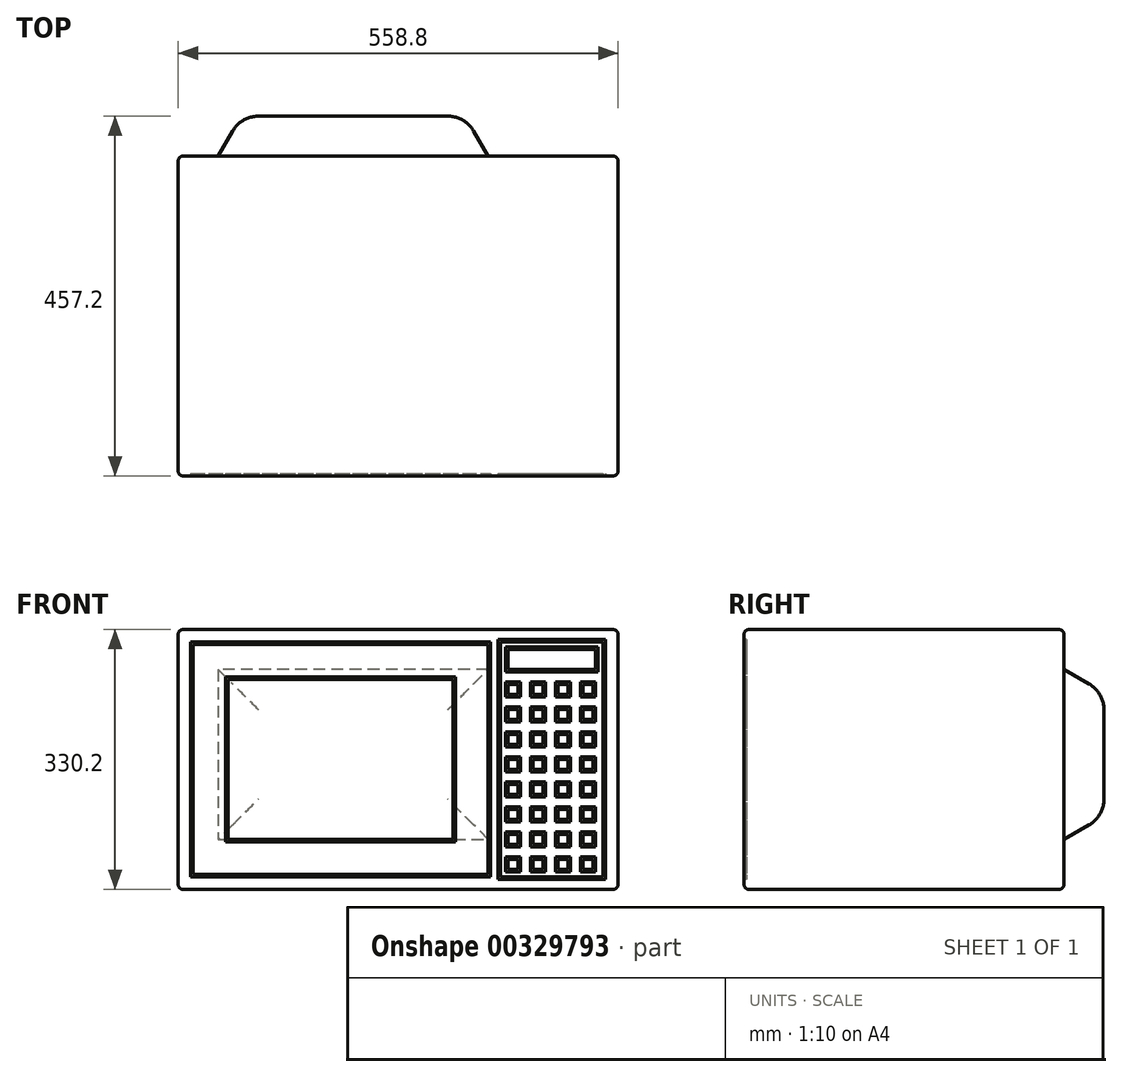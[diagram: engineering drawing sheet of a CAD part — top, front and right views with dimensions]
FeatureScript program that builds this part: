
annotation { "Feature Type Name" : "Feature", "Feature Type Description" : "" }
export const myFeature = defineFeature(function(context is Context, id is Id, definition is map)
    precondition{}
    {
        {
            var Q0;
            Q0=qCreatedBy(makeId("Front.planeOp"),FACE);
            var sketch = newSketch(context, id + "F0", { "sketchPlane" : qUnion([Q0])});
            skLineSegment(sketch, "E0.bottom", {"start": v(0, 0) * mm, "end": v(-558.8, 0) * mm});
            skLineSegment(sketch, "E0.top", {"start": v(0, 330.2) * mm, "end": v(-558.8, 330.2) * mm});
            skLineSegment(sketch, "E0.left", {"start": v(0, 0) * mm, "end": v(0, 330.2) * mm});
            skLineSegment(sketch, "E0.right", {"start": v(-558.8, 0) * mm, "end": v(-558.8, 330.2) * mm});
            skSolve(sketch);
        }
        {
            var Q0;
            Q0 = qSketchRegion(id + "F0", true);
            extrude(context, id + "F1", {"entities" : qUnion([Q0]), "oppositeDirection" : true, "depth" : 406.4 * mm});
        }
        {
            var Q0;
            Q0=makeQuery(id+"F1.opExtrude","SWEPT_FACE",FACE,{"disambiguationData":[OSD([sQuery(id+"F0.wireOp",EDGE,"E0.top")])]});
            var Q1;
            Q1=makeQuery(id+"F1.opExtrude","SWEPT_FACE",FACE,{"disambiguationData":[OSD([sQuery(id+"F0.wireOp",EDGE,"E0.left")])]});
            var Q2;
            Q2=makeQuery(id+"F1.opExtrude","CAP_FACE",FACE,{"disambiguationData":[OSD([sQuery(id+"F0.wireOp",EDGE,"E0.bottom"),sQuery(id+"F0.wireOp",EDGE,"E0.top"),sQuery(id+"F0.wireOp",EDGE,"E0.left"),sQuery(id+"F0.wireOp",EDGE,"E0.right")])],"isStart":false});
            var Q3;
            Q3=makeQuery(id+"F1.opExtrude","CAP_FACE",FACE,{"disambiguationData":[OSD([sQuery(id+"F0.wireOp",EDGE,"E0.bottom"),sQuery(id+"F0.wireOp",EDGE,"E0.top"),sQuery(id+"F0.wireOp",EDGE,"E0.left"),sQuery(id+"F0.wireOp",EDGE,"E0.right")])],"isStart":true});
            var Q4;
            Q4=makeQuery(id+"F1.opExtrude","SWEPT_FACE",FACE,{"disambiguationData":[OSD([sQuery(id+"F0.wireOp",EDGE,"E0.right")])]});
            fillet(context, id + "F2", {"entities" : qUnion([Q0, Q1, Q2, Q3, Q4]), "radius" : 6.35 * mm, "tangentPropagation" : true, "allowEdgeOverflow" : false});
        }
        {
            var Q0;
            Q0=makeQuery(id+"F1.opExtrude","CAP_FACE",FACE,{"disambiguationData":[OSD([sQuery(id+"F0.wireOp",EDGE,"E0.bottom"),sQuery(id+"F0.wireOp",EDGE,"E0.top"),sQuery(id+"F0.wireOp",EDGE,"E0.left"),sQuery(id+"F0.wireOp",EDGE,"E0.right")])],"isStart":false});
            var sketch = newSketch(context, id + "F3", { "sketchPlane" : qUnion([Q0])});
            skLineSegment(sketch, "E1.bottom", {"start": v(508, 279.4) * mm, "end": v(165.1, 279.4) * mm});
            skLineSegment(sketch, "E1.top", {"start": v(508, 63.5) * mm, "end": v(165.1, 63.5) * mm});
            skLineSegment(sketch, "E1.left", {"start": v(508, 279.4) * mm, "end": v(508, 63.5) * mm});
            skLineSegment(sketch, "E1.right", {"start": v(165.1, 279.4) * mm, "end": v(165.1, 63.5) * mm});
            skSolve(sketch);
        }
        {
            var Q0;
            Q0 = qSketchRegion(id + "F3", true);
            extrude(context, id + "F4", {"entities" : qUnion([Q0]), "operationType" : NewBodyOperationType.ADD, "depth" : 50.8 * mm, "hasDraft" : true, "draftAngle" : 30 * degree, "draftPullDirection" : true});
        }
        {
            var Q0;
            Q0=makeQuery(id+"F4.opExtrude","CAP_FACE",FACE,{"disambiguationData":[OSD([sQuery(id+"F3.wireOp",EDGE,"E1.bottom"),sQuery(id+"F3.wireOp",EDGE,"E1.top"),sQuery(id+"F3.wireOp",EDGE,"E1.left"),sQuery(id+"F3.wireOp",EDGE,"E1.right")])],"isStart":false});
            var Q1;
            Q1=makeQuery(id+"F4.opExtrude","CAP_EDGE",EDGE,{"disambiguationData":[OSD([sQuery(id+"F3.wireOp",EDGE,"E1.bottom")])],"isStart":true});
            var Q2;
            Q2=makeQuery(id+"F4.opExtrude","CAP_EDGE",EDGE,{"disambiguationData":[OSD([sQuery(id+"F3.wireOp",EDGE,"E1.left")])],"isStart":true});
            var Q3;
            Q3=makeQuery(id+"F4.opExtrude","CAP_EDGE",EDGE,{"disambiguationData":[OSD([sQuery(id+"F3.wireOp",EDGE,"E1.right")])],"isStart":true});
            var Q4;
            Q4=makeQuery(id+"F4.opExtrude","CAP_EDGE",EDGE,{"disambiguationData":[OSD([sQuery(id+"F3.wireOp",EDGE,"E1.top")])],"isStart":true});
            fillet(context, id + "F5", {"entities" : qUnion([Q0, Q1, Q2, Q3, Q4]), "radius" : 38.1 * mm, "tangentPropagation" : true, "allowEdgeOverflow" : false});
        }
        {
            var Q0;
            Q0=makeQuery(id+"F1.opExtrude","CAP_FACE",FACE,{"disambiguationData":[OSD([sQuery(id+"F0.wireOp",EDGE,"E0.bottom"),sQuery(id+"F0.wireOp",EDGE,"E0.top"),sQuery(id+"F0.wireOp",EDGE,"E0.left"),sQuery(id+"F0.wireOp",EDGE,"E0.right")])],"isStart":true});
            var sketch = newSketch(context, id + "F6", { "sketchPlane" : qUnion([Q0])});
            skLineSegment(sketch, "E2.bottom", {"start": v(-542.93, 314.33) * mm, "end": v(-161.93, 314.33) * mm});
            skLineSegment(sketch, "E2.top", {"start": v(-542.93, 15.88) * mm, "end": v(-161.92, 15.88) * mm});
            skLineSegment(sketch, "E2.left", {"start": v(-542.93, 314.32) * mm, "end": v(-542.93, 15.87) * mm});
            skLineSegment(sketch, "E2.right", {"start": v(-161.93, 314.33) * mm, "end": v(-161.92, 15.88) * mm});
            skLineSegment(sketch, "E3.bottom", {"start": v(-498.48, 269.88) * mm, "end": v(-206.38, 269.88) * mm});
            skLineSegment(sketch, "E3.top", {"start": v(-498.48, 60.32) * mm, "end": v(-206.37, 60.33) * mm});
            skLineSegment(sketch, "E3.left", {"start": v(-498.48, 269.88) * mm, "end": v(-498.48, 60.32) * mm});
            skLineSegment(sketch, "E3.right", {"start": v(-206.38, 269.88) * mm, "end": v(-206.37, 60.33) * mm});
            skLineSegment(sketch, "E4.bottom", {"start": v(-149.23, 314.33) * mm, "end": v(-19.05, 314.33) * mm});
            skLineSegment(sketch, "E4.top", {"start": v(-149.22, 15.88) * mm, "end": v(-19.05, 15.88) * mm});
            skLineSegment(sketch, "E4.left", {"start": v(-149.23, 314.33) * mm, "end": v(-149.22, 15.88) * mm});
            skLineSegment(sketch, "E4.right", {"start": v(-19.05, 314.33) * mm, "end": v(-19.05, 15.88) * mm});
            skLineSegment(sketch, "E5.bottom", {"start": v(-142.88, 307.98) * mm, "end": v(-25.4, 307.98) * mm});
            skLineSegment(sketch, "E5.top", {"start": v(-142.88, 276.23) * mm, "end": v(-25.4, 276.23) * mm});
            skLineSegment(sketch, "E5.left", {"start": v(-142.88, 307.98) * mm, "end": v(-142.88, 276.23) * mm});
            skLineSegment(sketch, "E5.right", {"start": v(-25.4, 307.98) * mm, "end": v(-25.4, 276.23) * mm});
            skLineSegment(sketch, "E6.bottom", {"start": v(-142.87, 41.28) * mm, "end": v(-123.83, 41.28) * mm});
            skLineSegment(sketch, "E6.top", {"start": v(-142.87, 22.23) * mm, "end": v(-123.83, 22.23) * mm});
            skLineSegment(sketch, "E6.left", {"start": v(-142.87, 41.28) * mm, "end": v(-142.87, 22.23) * mm});
            skLineSegment(sketch, "E6.right", {"start": v(-123.83, 41.28) * mm, "end": v(-123.83, 22.23) * mm});
            skLineSegment(sketch, "E7.0", {"start": v(-539.75, 311.15) * mm, "end": v(-539.75, 19.05) * mm});
            skLineSegment(sketch, "E7.1", {"start": v(-539.75, 311.15) * mm, "end": v(-165.1, 311.15) * mm});
            skLineSegment(sketch, "E7.2", {"start": v(-165.1, 311.15) * mm, "end": v(-165.1, 19.05) * mm});
            skLineSegment(sketch, "E7.3", {"start": v(-539.75, 19.05) * mm, "end": v(-165.1, 19.05) * mm});
            skLineSegment(sketch, "E8.0", {"start": v(-495.3, 266.7) * mm, "end": v(-209.55, 266.7) * mm});
            skLineSegment(sketch, "E8.1", {"start": v(-495.3, 266.7) * mm, "end": v(-495.3, 63.5) * mm});
            skLineSegment(sketch, "E8.2", {"start": v(-495.3, 63.5) * mm, "end": v(-209.55, 63.5) * mm});
            skLineSegment(sketch, "E8.3", {"start": v(-209.55, 266.7) * mm, "end": v(-209.55, 63.5) * mm});
            skLineSegment(sketch, "E9.0", {"start": v(-152.4, 317.5) * mm, "end": v(-15.88, 317.5) * mm});
            skLineSegment(sketch, "E9.1", {"start": v(-152.4, 317.5) * mm, "end": v(-152.4, 12.7) * mm});
            skLineSegment(sketch, "E9.2", {"start": v(-152.4, 12.7) * mm, "end": v(-15.88, 12.7) * mm});
            skLineSegment(sketch, "E9.3", {"start": v(-15.88, 317.5) * mm, "end": v(-15.88, 12.7) * mm});
            skLineSegment(sketch, "E10.0", {"start": v(-139.7, 279.4) * mm, "end": v(-28.58, 279.4) * mm});
            skLineSegment(sketch, "E10.1", {"start": v(-139.7, 304.8) * mm, "end": v(-139.7, 279.4) * mm});
            skLineSegment(sketch, "E10.2", {"start": v(-139.7, 304.8) * mm, "end": v(-28.58, 304.8) * mm});
            skLineSegment(sketch, "E10.3", {"start": v(-28.58, 304.8) * mm, "end": v(-28.58, 279.4) * mm});
            skLineSegment(sketch, "E11.0", {"start": v(-127, 38.1) * mm, "end": v(-127, 25.4) * mm});
            skLineSegment(sketch, "E11.1", {"start": v(-139.7, 38.1) * mm, "end": v(-127, 38.1) * mm});
            skLineSegment(sketch, "E11.2", {"start": v(-139.7, 38.1) * mm, "end": v(-139.7, 25.4) * mm});
            skLineSegment(sketch, "E11.3", {"start": v(-139.7, 25.4) * mm, "end": v(-127, 25.4) * mm});
            skLineSegment(sketch, "E12.0.1.0", {"start": v(-142.87, 73.03) * mm, "end": v(-142.87, 53.98) * mm});
            skLineSegment(sketch, "E12.0.1.1", {"start": v(-139.7, 69.85) * mm, "end": v(-139.7, 57.15) * mm});
            skLineSegment(sketch, "E12.0.1.2", {"start": v(-142.87, 73.03) * mm, "end": v(-123.83, 73.03) * mm});
            skLineSegment(sketch, "E12.0.1.3", {"start": v(-139.7, 69.85) * mm, "end": v(-127, 69.85) * mm});
            skLineSegment(sketch, "E12.0.1.4", {"start": v(-123.83, 73.03) * mm, "end": v(-123.83, 53.98) * mm});
            skLineSegment(sketch, "E12.0.1.5", {"start": v(-127, 69.85) * mm, "end": v(-127, 57.15) * mm});
            skLineSegment(sketch, "E12.0.1.6", {"start": v(-139.7, 57.15) * mm, "end": v(-127, 57.15) * mm});
            skLineSegment(sketch, "E12.0.1.7", {"start": v(-142.87, 53.98) * mm, "end": v(-123.83, 53.98) * mm});
            skLineSegment(sketch, "E12.0.2.0", {"start": v(-142.87, 104.78) * mm, "end": v(-142.87, 85.73) * mm});
            skLineSegment(sketch, "E12.0.2.1", {"start": v(-139.7, 101.6) * mm, "end": v(-139.7, 88.9) * mm});
            skLineSegment(sketch, "E12.0.2.2", {"start": v(-142.87, 104.78) * mm, "end": v(-123.83, 104.78) * mm});
            skLineSegment(sketch, "E12.0.2.3", {"start": v(-139.7, 101.6) * mm, "end": v(-127, 101.6) * mm});
            skLineSegment(sketch, "E12.0.2.4", {"start": v(-123.83, 104.78) * mm, "end": v(-123.83, 85.73) * mm});
            skLineSegment(sketch, "E12.0.2.5", {"start": v(-127, 101.6) * mm, "end": v(-127, 88.9) * mm});
            skLineSegment(sketch, "E12.0.2.6", {"start": v(-139.7, 88.9) * mm, "end": v(-127, 88.9) * mm});
            skLineSegment(sketch, "E12.0.2.7", {"start": v(-142.87, 85.73) * mm, "end": v(-123.83, 85.73) * mm});
            skLineSegment(sketch, "E12.0.3.0", {"start": v(-142.87, 136.53) * mm, "end": v(-142.87, 117.48) * mm});
            skLineSegment(sketch, "E12.0.3.1", {"start": v(-139.7, 133.35) * mm, "end": v(-139.7, 120.65) * mm});
            skLineSegment(sketch, "E12.0.3.2", {"start": v(-142.87, 136.53) * mm, "end": v(-123.83, 136.53) * mm});
            skLineSegment(sketch, "E12.0.3.3", {"start": v(-139.7, 133.35) * mm, "end": v(-127, 133.35) * mm});
            skLineSegment(sketch, "E12.0.3.4", {"start": v(-123.83, 136.53) * mm, "end": v(-123.83, 117.48) * mm});
            skLineSegment(sketch, "E12.0.3.5", {"start": v(-127, 133.35) * mm, "end": v(-127, 120.65) * mm});
            skLineSegment(sketch, "E12.0.3.6", {"start": v(-139.7, 120.65) * mm, "end": v(-127, 120.65) * mm});
            skLineSegment(sketch, "E12.0.3.7", {"start": v(-142.87, 117.48) * mm, "end": v(-123.83, 117.48) * mm});
            skLineSegment(sketch, "E12.0.4.0", {"start": v(-142.87, 168.28) * mm, "end": v(-142.87, 149.23) * mm});
            skLineSegment(sketch, "E12.0.4.1", {"start": v(-139.7, 165.1) * mm, "end": v(-139.7, 152.4) * mm});
            skLineSegment(sketch, "E12.0.4.2", {"start": v(-142.87, 168.28) * mm, "end": v(-123.83, 168.28) * mm});
            skLineSegment(sketch, "E12.0.4.3", {"start": v(-139.7, 165.1) * mm, "end": v(-127, 165.1) * mm});
            skLineSegment(sketch, "E12.0.4.4", {"start": v(-123.83, 168.28) * mm, "end": v(-123.83, 149.23) * mm});
            skLineSegment(sketch, "E12.0.4.5", {"start": v(-127, 165.1) * mm, "end": v(-127, 152.4) * mm});
            skLineSegment(sketch, "E12.0.4.6", {"start": v(-139.7, 152.4) * mm, "end": v(-127, 152.4) * mm});
            skLineSegment(sketch, "E12.0.4.7", {"start": v(-142.87, 149.23) * mm, "end": v(-123.83, 149.23) * mm});
            skLineSegment(sketch, "E12.0.5.0", {"start": v(-142.87, 200.03) * mm, "end": v(-142.87, 180.98) * mm});
            skLineSegment(sketch, "E12.0.5.1", {"start": v(-139.7, 196.85) * mm, "end": v(-139.7, 184.15) * mm});
            skLineSegment(sketch, "E12.0.5.2", {"start": v(-142.87, 200.03) * mm, "end": v(-123.83, 200.03) * mm});
            skLineSegment(sketch, "E12.0.5.3", {"start": v(-139.7, 196.85) * mm, "end": v(-127, 196.85) * mm});
            skLineSegment(sketch, "E12.0.5.4", {"start": v(-123.83, 200.03) * mm, "end": v(-123.83, 180.98) * mm});
            skLineSegment(sketch, "E12.0.5.5", {"start": v(-127, 196.85) * mm, "end": v(-127, 184.15) * mm});
            skLineSegment(sketch, "E12.0.5.6", {"start": v(-139.7, 184.15) * mm, "end": v(-127, 184.15) * mm});
            skLineSegment(sketch, "E12.0.5.7", {"start": v(-142.87, 180.98) * mm, "end": v(-123.83, 180.98) * mm});
            skLineSegment(sketch, "E12.0.6.0", {"start": v(-142.87, 231.78) * mm, "end": v(-142.87, 212.73) * mm});
            skLineSegment(sketch, "E12.0.6.1", {"start": v(-139.7, 228.6) * mm, "end": v(-139.7, 215.9) * mm});
            skLineSegment(sketch, "E12.0.6.2", {"start": v(-142.87, 231.78) * mm, "end": v(-123.83, 231.78) * mm});
            skLineSegment(sketch, "E12.0.6.3", {"start": v(-139.7, 228.6) * mm, "end": v(-127, 228.6) * mm});
            skLineSegment(sketch, "E12.0.6.4", {"start": v(-123.83, 231.78) * mm, "end": v(-123.83, 212.73) * mm});
            skLineSegment(sketch, "E12.0.6.5", {"start": v(-127, 228.6) * mm, "end": v(-127, 215.9) * mm});
            skLineSegment(sketch, "E12.0.6.6", {"start": v(-139.7, 215.9) * mm, "end": v(-127, 215.9) * mm});
            skLineSegment(sketch, "E12.0.6.7", {"start": v(-142.87, 212.73) * mm, "end": v(-123.83, 212.73) * mm});
            skLineSegment(sketch, "E12.0.7.0", {"start": v(-142.87, 263.53) * mm, "end": v(-142.87, 244.48) * mm});
            skLineSegment(sketch, "E12.0.7.1", {"start": v(-139.7, 260.35) * mm, "end": v(-139.7, 247.65) * mm});
            skLineSegment(sketch, "E12.0.7.2", {"start": v(-142.87, 263.53) * mm, "end": v(-123.83, 263.53) * mm});
            skLineSegment(sketch, "E12.0.7.3", {"start": v(-139.7, 260.35) * mm, "end": v(-127, 260.35) * mm});
            skLineSegment(sketch, "E12.0.7.4", {"start": v(-123.83, 263.53) * mm, "end": v(-123.83, 244.48) * mm});
            skLineSegment(sketch, "E12.0.7.5", {"start": v(-127, 260.35) * mm, "end": v(-127, 247.65) * mm});
            skLineSegment(sketch, "E12.0.7.6", {"start": v(-139.7, 247.65) * mm, "end": v(-127, 247.65) * mm});
            skLineSegment(sketch, "E12.0.7.7", {"start": v(-142.87, 244.48) * mm, "end": v(-123.83, 244.48) * mm});
            skLineSegment(sketch, "E12.1.0.0", {"start": v(-111.12, 41.28) * mm, "end": v(-111.12, 22.23) * mm});
            skLineSegment(sketch, "E12.1.0.1", {"start": v(-107.95, 38.1) * mm, "end": v(-107.95, 25.4) * mm});
            skLineSegment(sketch, "E12.1.0.2", {"start": v(-111.12, 41.28) * mm, "end": v(-92.08, 41.28) * mm});
            skLineSegment(sketch, "E12.1.0.3", {"start": v(-107.95, 38.1) * mm, "end": v(-95.25, 38.1) * mm});
            skLineSegment(sketch, "E12.1.0.4", {"start": v(-92.08, 41.28) * mm, "end": v(-92.08, 22.23) * mm});
            skLineSegment(sketch, "E12.1.0.5", {"start": v(-95.25, 38.1) * mm, "end": v(-95.25, 25.4) * mm});
            skLineSegment(sketch, "E12.1.0.6", {"start": v(-107.95, 25.4) * mm, "end": v(-95.25, 25.4) * mm});
            skLineSegment(sketch, "E12.1.0.7", {"start": v(-111.12, 22.23) * mm, "end": v(-92.08, 22.23) * mm});
            skLineSegment(sketch, "E12.1.1.0", {"start": v(-111.12, 73.03) * mm, "end": v(-111.12, 53.98) * mm});
            skLineSegment(sketch, "E12.1.1.1", {"start": v(-107.95, 69.85) * mm, "end": v(-107.95, 57.15) * mm});
            skLineSegment(sketch, "E12.1.1.2", {"start": v(-111.12, 73.03) * mm, "end": v(-92.08, 73.03) * mm});
            skLineSegment(sketch, "E12.1.1.3", {"start": v(-107.95, 69.85) * mm, "end": v(-95.25, 69.85) * mm});
            skLineSegment(sketch, "E12.1.1.4", {"start": v(-92.08, 73.03) * mm, "end": v(-92.08, 53.98) * mm});
            skLineSegment(sketch, "E12.1.1.5", {"start": v(-95.25, 69.85) * mm, "end": v(-95.25, 57.15) * mm});
            skLineSegment(sketch, "E12.1.1.6", {"start": v(-107.95, 57.15) * mm, "end": v(-95.25, 57.15) * mm});
            skLineSegment(sketch, "E12.1.1.7", {"start": v(-111.12, 53.98) * mm, "end": v(-92.08, 53.98) * mm});
            skLineSegment(sketch, "E12.1.2.0", {"start": v(-111.12, 104.78) * mm, "end": v(-111.12, 85.73) * mm});
            skLineSegment(sketch, "E12.1.2.1", {"start": v(-107.95, 101.6) * mm, "end": v(-107.95, 88.9) * mm});
            skLineSegment(sketch, "E12.1.2.2", {"start": v(-111.12, 104.78) * mm, "end": v(-92.08, 104.78) * mm});
            skLineSegment(sketch, "E12.1.2.3", {"start": v(-107.95, 101.6) * mm, "end": v(-95.25, 101.6) * mm});
            skLineSegment(sketch, "E12.1.2.4", {"start": v(-92.08, 104.78) * mm, "end": v(-92.08, 85.73) * mm});
            skLineSegment(sketch, "E12.1.2.5", {"start": v(-95.25, 101.6) * mm, "end": v(-95.25, 88.9) * mm});
            skLineSegment(sketch, "E12.1.2.6", {"start": v(-107.95, 88.9) * mm, "end": v(-95.25, 88.9) * mm});
            skLineSegment(sketch, "E12.1.2.7", {"start": v(-111.12, 85.73) * mm, "end": v(-92.08, 85.73) * mm});
            skLineSegment(sketch, "E12.1.3.0", {"start": v(-111.12, 136.53) * mm, "end": v(-111.12, 117.48) * mm});
            skLineSegment(sketch, "E12.1.3.1", {"start": v(-107.95, 133.35) * mm, "end": v(-107.95, 120.65) * mm});
            skLineSegment(sketch, "E12.1.3.2", {"start": v(-111.12, 136.53) * mm, "end": v(-92.08, 136.53) * mm});
            skLineSegment(sketch, "E12.1.3.3", {"start": v(-107.95, 133.35) * mm, "end": v(-95.25, 133.35) * mm});
            skLineSegment(sketch, "E12.1.3.4", {"start": v(-92.08, 136.53) * mm, "end": v(-92.08, 117.48) * mm});
            skLineSegment(sketch, "E12.1.3.5", {"start": v(-95.25, 133.35) * mm, "end": v(-95.25, 120.65) * mm});
            skLineSegment(sketch, "E12.1.3.6", {"start": v(-107.95, 120.65) * mm, "end": v(-95.25, 120.65) * mm});
            skLineSegment(sketch, "E12.1.3.7", {"start": v(-111.12, 117.48) * mm, "end": v(-92.08, 117.48) * mm});
            skLineSegment(sketch, "E12.1.4.0", {"start": v(-111.12, 168.28) * mm, "end": v(-111.12, 149.23) * mm});
            skLineSegment(sketch, "E12.1.4.1", {"start": v(-107.95, 165.1) * mm, "end": v(-107.95, 152.4) * mm});
            skLineSegment(sketch, "E12.1.4.2", {"start": v(-111.12, 168.28) * mm, "end": v(-92.08, 168.28) * mm});
            skLineSegment(sketch, "E12.1.4.3", {"start": v(-107.95, 165.1) * mm, "end": v(-95.25, 165.1) * mm});
            skLineSegment(sketch, "E12.1.4.4", {"start": v(-92.08, 168.28) * mm, "end": v(-92.08, 149.23) * mm});
            skLineSegment(sketch, "E12.1.4.5", {"start": v(-95.25, 165.1) * mm, "end": v(-95.25, 152.4) * mm});
            skLineSegment(sketch, "E12.1.4.6", {"start": v(-107.95, 152.4) * mm, "end": v(-95.25, 152.4) * mm});
            skLineSegment(sketch, "E12.1.4.7", {"start": v(-111.12, 149.23) * mm, "end": v(-92.08, 149.23) * mm});
            skLineSegment(sketch, "E12.1.5.0", {"start": v(-111.12, 200.03) * mm, "end": v(-111.12, 180.98) * mm});
            skLineSegment(sketch, "E12.1.5.1", {"start": v(-107.95, 196.85) * mm, "end": v(-107.95, 184.15) * mm});
            skLineSegment(sketch, "E12.1.5.2", {"start": v(-111.12, 200.03) * mm, "end": v(-92.08, 200.03) * mm});
            skLineSegment(sketch, "E12.1.5.3", {"start": v(-107.95, 196.85) * mm, "end": v(-95.25, 196.85) * mm});
            skLineSegment(sketch, "E12.1.5.4", {"start": v(-92.08, 200.03) * mm, "end": v(-92.08, 180.98) * mm});
            skLineSegment(sketch, "E12.1.5.5", {"start": v(-95.25, 196.85) * mm, "end": v(-95.25, 184.15) * mm});
            skLineSegment(sketch, "E12.1.5.6", {"start": v(-107.95, 184.15) * mm, "end": v(-95.25, 184.15) * mm});
            skLineSegment(sketch, "E12.1.5.7", {"start": v(-111.12, 180.98) * mm, "end": v(-92.08, 180.98) * mm});
            skLineSegment(sketch, "E12.1.6.0", {"start": v(-111.12, 231.78) * mm, "end": v(-111.12, 212.73) * mm});
            skLineSegment(sketch, "E12.1.6.1", {"start": v(-107.95, 228.6) * mm, "end": v(-107.95, 215.9) * mm});
            skLineSegment(sketch, "E12.1.6.2", {"start": v(-111.12, 231.78) * mm, "end": v(-92.08, 231.78) * mm});
            skLineSegment(sketch, "E12.1.6.3", {"start": v(-107.95, 228.6) * mm, "end": v(-95.25, 228.6) * mm});
            skLineSegment(sketch, "E12.1.6.4", {"start": v(-92.08, 231.78) * mm, "end": v(-92.08, 212.73) * mm});
            skLineSegment(sketch, "E12.1.6.5", {"start": v(-95.25, 228.6) * mm, "end": v(-95.25, 215.9) * mm});
            skLineSegment(sketch, "E12.1.6.6", {"start": v(-107.95, 215.9) * mm, "end": v(-95.25, 215.9) * mm});
            skLineSegment(sketch, "E12.1.6.7", {"start": v(-111.12, 212.73) * mm, "end": v(-92.08, 212.73) * mm});
            skLineSegment(sketch, "E12.1.7.0", {"start": v(-111.12, 263.53) * mm, "end": v(-111.12, 244.48) * mm});
            skLineSegment(sketch, "E12.1.7.1", {"start": v(-107.95, 260.35) * mm, "end": v(-107.95, 247.65) * mm});
            skLineSegment(sketch, "E12.1.7.2", {"start": v(-111.12, 263.53) * mm, "end": v(-92.08, 263.53) * mm});
            skLineSegment(sketch, "E12.1.7.3", {"start": v(-107.95, 260.35) * mm, "end": v(-95.25, 260.35) * mm});
            skLineSegment(sketch, "E12.1.7.4", {"start": v(-92.08, 263.53) * mm, "end": v(-92.08, 244.48) * mm});
            skLineSegment(sketch, "E12.1.7.5", {"start": v(-95.25, 260.35) * mm, "end": v(-95.25, 247.65) * mm});
            skLineSegment(sketch, "E12.1.7.6", {"start": v(-107.95, 247.65) * mm, "end": v(-95.25, 247.65) * mm});
            skLineSegment(sketch, "E12.1.7.7", {"start": v(-111.12, 244.48) * mm, "end": v(-92.08, 244.48) * mm});
            skLineSegment(sketch, "E12.2.0.0", {"start": v(-79.37, 41.28) * mm, "end": v(-79.37, 22.23) * mm});
            skLineSegment(sketch, "E12.2.0.1", {"start": v(-76.2, 38.1) * mm, "end": v(-76.2, 25.4) * mm});
            skLineSegment(sketch, "E12.2.0.2", {"start": v(-79.37, 41.28) * mm, "end": v(-60.33, 41.28) * mm});
            skLineSegment(sketch, "E12.2.0.3", {"start": v(-76.2, 38.1) * mm, "end": v(-63.5, 38.1) * mm});
            skLineSegment(sketch, "E12.2.0.4", {"start": v(-60.33, 41.28) * mm, "end": v(-60.33, 22.23) * mm});
            skLineSegment(sketch, "E12.2.0.5", {"start": v(-63.5, 38.1) * mm, "end": v(-63.5, 25.4) * mm});
            skLineSegment(sketch, "E12.2.0.6", {"start": v(-76.2, 25.4) * mm, "end": v(-63.5, 25.4) * mm});
            skLineSegment(sketch, "E12.2.0.7", {"start": v(-79.37, 22.23) * mm, "end": v(-60.33, 22.23) * mm});
            skLineSegment(sketch, "E12.2.1.0", {"start": v(-79.37, 73.03) * mm, "end": v(-79.37, 53.98) * mm});
            skLineSegment(sketch, "E12.2.1.1", {"start": v(-76.2, 69.85) * mm, "end": v(-76.2, 57.15) * mm});
            skLineSegment(sketch, "E12.2.1.2", {"start": v(-79.37, 73.03) * mm, "end": v(-60.33, 73.03) * mm});
            skLineSegment(sketch, "E12.2.1.3", {"start": v(-76.2, 69.85) * mm, "end": v(-63.5, 69.85) * mm});
            skLineSegment(sketch, "E12.2.1.4", {"start": v(-60.33, 73.03) * mm, "end": v(-60.33, 53.98) * mm});
            skLineSegment(sketch, "E12.2.1.5", {"start": v(-63.5, 69.85) * mm, "end": v(-63.5, 57.15) * mm});
            skLineSegment(sketch, "E12.2.1.6", {"start": v(-76.2, 57.15) * mm, "end": v(-63.5, 57.15) * mm});
            skLineSegment(sketch, "E12.2.1.7", {"start": v(-79.37, 53.98) * mm, "end": v(-60.33, 53.98) * mm});
            skLineSegment(sketch, "E12.2.2.0", {"start": v(-79.37, 104.78) * mm, "end": v(-79.37, 85.73) * mm});
            skLineSegment(sketch, "E12.2.2.1", {"start": v(-76.2, 101.6) * mm, "end": v(-76.2, 88.9) * mm});
            skLineSegment(sketch, "E12.2.2.2", {"start": v(-79.37, 104.78) * mm, "end": v(-60.33, 104.78) * mm});
            skLineSegment(sketch, "E12.2.2.3", {"start": v(-76.2, 101.6) * mm, "end": v(-63.5, 101.6) * mm});
            skLineSegment(sketch, "E12.2.2.4", {"start": v(-60.33, 104.78) * mm, "end": v(-60.33, 85.73) * mm});
            skLineSegment(sketch, "E12.2.2.5", {"start": v(-63.5, 101.6) * mm, "end": v(-63.5, 88.9) * mm});
            skLineSegment(sketch, "E12.2.2.6", {"start": v(-76.2, 88.9) * mm, "end": v(-63.5, 88.9) * mm});
            skLineSegment(sketch, "E12.2.2.7", {"start": v(-79.37, 85.73) * mm, "end": v(-60.33, 85.73) * mm});
            skLineSegment(sketch, "E12.2.3.0", {"start": v(-79.37, 136.53) * mm, "end": v(-79.37, 117.48) * mm});
            skLineSegment(sketch, "E12.2.3.1", {"start": v(-76.2, 133.35) * mm, "end": v(-76.2, 120.65) * mm});
            skLineSegment(sketch, "E12.2.3.2", {"start": v(-79.37, 136.53) * mm, "end": v(-60.33, 136.53) * mm});
            skLineSegment(sketch, "E12.2.3.3", {"start": v(-76.2, 133.35) * mm, "end": v(-63.5, 133.35) * mm});
            skLineSegment(sketch, "E12.2.3.4", {"start": v(-60.33, 136.53) * mm, "end": v(-60.33, 117.48) * mm});
            skLineSegment(sketch, "E12.2.3.5", {"start": v(-63.5, 133.35) * mm, "end": v(-63.5, 120.65) * mm});
            skLineSegment(sketch, "E12.2.3.6", {"start": v(-76.2, 120.65) * mm, "end": v(-63.5, 120.65) * mm});
            skLineSegment(sketch, "E12.2.3.7", {"start": v(-79.37, 117.48) * mm, "end": v(-60.33, 117.48) * mm});
            skLineSegment(sketch, "E12.2.4.0", {"start": v(-79.37, 168.28) * mm, "end": v(-79.37, 149.23) * mm});
            skLineSegment(sketch, "E12.2.4.1", {"start": v(-76.2, 165.1) * mm, "end": v(-76.2, 152.4) * mm});
            skLineSegment(sketch, "E12.2.4.2", {"start": v(-79.37, 168.28) * mm, "end": v(-60.33, 168.28) * mm});
            skLineSegment(sketch, "E12.2.4.3", {"start": v(-76.2, 165.1) * mm, "end": v(-63.5, 165.1) * mm});
            skLineSegment(sketch, "E12.2.4.4", {"start": v(-60.33, 168.28) * mm, "end": v(-60.33, 149.23) * mm});
            skLineSegment(sketch, "E12.2.4.5", {"start": v(-63.5, 165.1) * mm, "end": v(-63.5, 152.4) * mm});
            skLineSegment(sketch, "E12.2.4.6", {"start": v(-76.2, 152.4) * mm, "end": v(-63.5, 152.4) * mm});
            skLineSegment(sketch, "E12.2.4.7", {"start": v(-79.37, 149.23) * mm, "end": v(-60.33, 149.23) * mm});
            skLineSegment(sketch, "E12.2.5.0", {"start": v(-79.37, 200.03) * mm, "end": v(-79.37, 180.98) * mm});
            skLineSegment(sketch, "E12.2.5.1", {"start": v(-76.2, 196.85) * mm, "end": v(-76.2, 184.15) * mm});
            skLineSegment(sketch, "E12.2.5.2", {"start": v(-79.37, 200.03) * mm, "end": v(-60.33, 200.03) * mm});
            skLineSegment(sketch, "E12.2.5.3", {"start": v(-76.2, 196.85) * mm, "end": v(-63.5, 196.85) * mm});
            skLineSegment(sketch, "E12.2.5.4", {"start": v(-60.33, 200.03) * mm, "end": v(-60.33, 180.98) * mm});
            skLineSegment(sketch, "E12.2.5.5", {"start": v(-63.5, 196.85) * mm, "end": v(-63.5, 184.15) * mm});
            skLineSegment(sketch, "E12.2.5.6", {"start": v(-76.2, 184.15) * mm, "end": v(-63.5, 184.15) * mm});
            skLineSegment(sketch, "E12.2.5.7", {"start": v(-79.37, 180.98) * mm, "end": v(-60.33, 180.98) * mm});
            skLineSegment(sketch, "E12.2.6.0", {"start": v(-79.37, 231.78) * mm, "end": v(-79.37, 212.73) * mm});
            skLineSegment(sketch, "E12.2.6.1", {"start": v(-76.2, 228.6) * mm, "end": v(-76.2, 215.9) * mm});
            skLineSegment(sketch, "E12.2.6.2", {"start": v(-79.37, 231.78) * mm, "end": v(-60.33, 231.78) * mm});
            skLineSegment(sketch, "E12.2.6.3", {"start": v(-76.2, 228.6) * mm, "end": v(-63.5, 228.6) * mm});
            skLineSegment(sketch, "E12.2.6.4", {"start": v(-60.33, 231.78) * mm, "end": v(-60.33, 212.73) * mm});
            skLineSegment(sketch, "E12.2.6.5", {"start": v(-63.5, 228.6) * mm, "end": v(-63.5, 215.9) * mm});
            skLineSegment(sketch, "E12.2.6.6", {"start": v(-76.2, 215.9) * mm, "end": v(-63.5, 215.9) * mm});
            skLineSegment(sketch, "E12.2.6.7", {"start": v(-79.37, 212.73) * mm, "end": v(-60.33, 212.73) * mm});
            skLineSegment(sketch, "E12.2.7.0", {"start": v(-79.37, 263.53) * mm, "end": v(-79.37, 244.48) * mm});
            skLineSegment(sketch, "E12.2.7.1", {"start": v(-76.2, 260.35) * mm, "end": v(-76.2, 247.65) * mm});
            skLineSegment(sketch, "E12.2.7.2", {"start": v(-79.37, 263.53) * mm, "end": v(-60.33, 263.53) * mm});
            skLineSegment(sketch, "E12.2.7.3", {"start": v(-76.2, 260.35) * mm, "end": v(-63.5, 260.35) * mm});
            skLineSegment(sketch, "E12.2.7.4", {"start": v(-60.33, 263.53) * mm, "end": v(-60.33, 244.48) * mm});
            skLineSegment(sketch, "E12.2.7.5", {"start": v(-63.5, 260.35) * mm, "end": v(-63.5, 247.65) * mm});
            skLineSegment(sketch, "E12.2.7.6", {"start": v(-76.2, 247.65) * mm, "end": v(-63.5, 247.65) * mm});
            skLineSegment(sketch, "E12.2.7.7", {"start": v(-79.37, 244.48) * mm, "end": v(-60.33, 244.48) * mm});
            skLineSegment(sketch, "E12.3.0.0", {"start": v(-47.62, 41.28) * mm, "end": v(-47.62, 22.23) * mm});
            skLineSegment(sketch, "E12.3.0.1", {"start": v(-44.45, 38.1) * mm, "end": v(-44.45, 25.4) * mm});
            skLineSegment(sketch, "E12.3.0.2", {"start": v(-47.62, 41.28) * mm, "end": v(-28.58, 41.28) * mm});
            skLineSegment(sketch, "E12.3.0.3", {"start": v(-44.45, 38.1) * mm, "end": v(-31.75, 38.1) * mm});
            skLineSegment(sketch, "E12.3.0.4", {"start": v(-28.58, 41.28) * mm, "end": v(-28.58, 22.23) * mm});
            skLineSegment(sketch, "E12.3.0.5", {"start": v(-31.75, 38.1) * mm, "end": v(-31.75, 25.4) * mm});
            skLineSegment(sketch, "E12.3.0.6", {"start": v(-44.45, 25.4) * mm, "end": v(-31.75, 25.4) * mm});
            skLineSegment(sketch, "E12.3.0.7", {"start": v(-47.62, 22.23) * mm, "end": v(-28.58, 22.23) * mm});
            skLineSegment(sketch, "E12.3.1.0", {"start": v(-47.62, 73.03) * mm, "end": v(-47.62, 53.98) * mm});
            skLineSegment(sketch, "E12.3.1.1", {"start": v(-44.45, 69.85) * mm, "end": v(-44.45, 57.15) * mm});
            skLineSegment(sketch, "E12.3.1.2", {"start": v(-47.62, 73.03) * mm, "end": v(-28.58, 73.03) * mm});
            skLineSegment(sketch, "E12.3.1.3", {"start": v(-44.45, 69.85) * mm, "end": v(-31.75, 69.85) * mm});
            skLineSegment(sketch, "E12.3.1.4", {"start": v(-28.58, 73.03) * mm, "end": v(-28.58, 53.98) * mm});
            skLineSegment(sketch, "E12.3.1.5", {"start": v(-31.75, 69.85) * mm, "end": v(-31.75, 57.15) * mm});
            skLineSegment(sketch, "E12.3.1.6", {"start": v(-44.45, 57.15) * mm, "end": v(-31.75, 57.15) * mm});
            skLineSegment(sketch, "E12.3.1.7", {"start": v(-47.62, 53.98) * mm, "end": v(-28.58, 53.98) * mm});
            skLineSegment(sketch, "E12.3.2.0", {"start": v(-47.62, 104.78) * mm, "end": v(-47.62, 85.73) * mm});
            skLineSegment(sketch, "E12.3.2.1", {"start": v(-44.45, 101.6) * mm, "end": v(-44.45, 88.9) * mm});
            skLineSegment(sketch, "E12.3.2.2", {"start": v(-47.62, 104.78) * mm, "end": v(-28.58, 104.78) * mm});
            skLineSegment(sketch, "E12.3.2.3", {"start": v(-44.45, 101.6) * mm, "end": v(-31.75, 101.6) * mm});
            skLineSegment(sketch, "E12.3.2.4", {"start": v(-28.58, 104.78) * mm, "end": v(-28.58, 85.73) * mm});
            skLineSegment(sketch, "E12.3.2.5", {"start": v(-31.75, 101.6) * mm, "end": v(-31.75, 88.9) * mm});
            skLineSegment(sketch, "E12.3.2.6", {"start": v(-44.45, 88.9) * mm, "end": v(-31.75, 88.9) * mm});
            skLineSegment(sketch, "E12.3.2.7", {"start": v(-47.62, 85.73) * mm, "end": v(-28.58, 85.73) * mm});
            skLineSegment(sketch, "E12.3.3.0", {"start": v(-47.62, 136.53) * mm, "end": v(-47.62, 117.48) * mm});
            skLineSegment(sketch, "E12.3.3.1", {"start": v(-44.45, 133.35) * mm, "end": v(-44.45, 120.65) * mm});
            skLineSegment(sketch, "E12.3.3.2", {"start": v(-47.62, 136.53) * mm, "end": v(-28.58, 136.53) * mm});
            skLineSegment(sketch, "E12.3.3.3", {"start": v(-44.45, 133.35) * mm, "end": v(-31.75, 133.35) * mm});
            skLineSegment(sketch, "E12.3.3.4", {"start": v(-28.58, 136.53) * mm, "end": v(-28.58, 117.48) * mm});
            skLineSegment(sketch, "E12.3.3.5", {"start": v(-31.75, 133.35) * mm, "end": v(-31.75, 120.65) * mm});
            skLineSegment(sketch, "E12.3.3.6", {"start": v(-44.45, 120.65) * mm, "end": v(-31.75, 120.65) * mm});
            skLineSegment(sketch, "E12.3.3.7", {"start": v(-47.62, 117.48) * mm, "end": v(-28.58, 117.48) * mm});
            skLineSegment(sketch, "E12.3.4.0", {"start": v(-47.62, 168.28) * mm, "end": v(-47.62, 149.23) * mm});
            skLineSegment(sketch, "E12.3.4.1", {"start": v(-44.45, 165.1) * mm, "end": v(-44.45, 152.4) * mm});
            skLineSegment(sketch, "E12.3.4.2", {"start": v(-47.62, 168.28) * mm, "end": v(-28.58, 168.28) * mm});
            skLineSegment(sketch, "E12.3.4.3", {"start": v(-44.45, 165.1) * mm, "end": v(-31.75, 165.1) * mm});
            skLineSegment(sketch, "E12.3.4.4", {"start": v(-28.58, 168.28) * mm, "end": v(-28.58, 149.23) * mm});
            skLineSegment(sketch, "E12.3.4.5", {"start": v(-31.75, 165.1) * mm, "end": v(-31.75, 152.4) * mm});
            skLineSegment(sketch, "E12.3.4.6", {"start": v(-44.45, 152.4) * mm, "end": v(-31.75, 152.4) * mm});
            skLineSegment(sketch, "E12.3.4.7", {"start": v(-47.62, 149.23) * mm, "end": v(-28.58, 149.23) * mm});
            skLineSegment(sketch, "E12.3.5.0", {"start": v(-47.62, 200.03) * mm, "end": v(-47.62, 180.98) * mm});
            skLineSegment(sketch, "E12.3.5.1", {"start": v(-44.45, 196.85) * mm, "end": v(-44.45, 184.15) * mm});
            skLineSegment(sketch, "E12.3.5.2", {"start": v(-47.62, 200.03) * mm, "end": v(-28.58, 200.03) * mm});
            skLineSegment(sketch, "E12.3.5.3", {"start": v(-44.45, 196.85) * mm, "end": v(-31.75, 196.85) * mm});
            skLineSegment(sketch, "E12.3.5.4", {"start": v(-28.58, 200.03) * mm, "end": v(-28.58, 180.98) * mm});
            skLineSegment(sketch, "E12.3.5.5", {"start": v(-31.75, 196.85) * mm, "end": v(-31.75, 184.15) * mm});
            skLineSegment(sketch, "E12.3.5.6", {"start": v(-44.45, 184.15) * mm, "end": v(-31.75, 184.15) * mm});
            skLineSegment(sketch, "E12.3.5.7", {"start": v(-47.62, 180.98) * mm, "end": v(-28.58, 180.98) * mm});
            skLineSegment(sketch, "E12.3.6.0", {"start": v(-47.62, 231.78) * mm, "end": v(-47.62, 212.73) * mm});
            skLineSegment(sketch, "E12.3.6.1", {"start": v(-44.45, 228.6) * mm, "end": v(-44.45, 215.9) * mm});
            skLineSegment(sketch, "E12.3.6.2", {"start": v(-47.62, 231.78) * mm, "end": v(-28.58, 231.78) * mm});
            skLineSegment(sketch, "E12.3.6.3", {"start": v(-44.45, 228.6) * mm, "end": v(-31.75, 228.6) * mm});
            skLineSegment(sketch, "E12.3.6.4", {"start": v(-28.58, 231.78) * mm, "end": v(-28.58, 212.73) * mm});
            skLineSegment(sketch, "E12.3.6.5", {"start": v(-31.75, 228.6) * mm, "end": v(-31.75, 215.9) * mm});
            skLineSegment(sketch, "E12.3.6.6", {"start": v(-44.45, 215.9) * mm, "end": v(-31.75, 215.9) * mm});
            skLineSegment(sketch, "E12.3.6.7", {"start": v(-47.62, 212.73) * mm, "end": v(-28.58, 212.73) * mm});
            skLineSegment(sketch, "E12.3.7.0", {"start": v(-47.62, 263.53) * mm, "end": v(-47.62, 244.48) * mm});
            skLineSegment(sketch, "E12.3.7.1", {"start": v(-44.45, 260.35) * mm, "end": v(-44.45, 247.65) * mm});
            skLineSegment(sketch, "E12.3.7.2", {"start": v(-47.62, 263.53) * mm, "end": v(-28.58, 263.53) * mm});
            skLineSegment(sketch, "E12.3.7.3", {"start": v(-44.45, 260.35) * mm, "end": v(-31.75, 260.35) * mm});
            skLineSegment(sketch, "E12.3.7.4", {"start": v(-28.58, 263.53) * mm, "end": v(-28.58, 244.48) * mm});
            skLineSegment(sketch, "E12.3.7.5", {"start": v(-31.75, 260.35) * mm, "end": v(-31.75, 247.65) * mm});
            skLineSegment(sketch, "E12.3.7.6", {"start": v(-44.45, 247.65) * mm, "end": v(-31.75, 247.65) * mm});
            skLineSegment(sketch, "E12.3.7.7", {"start": v(-47.62, 244.48) * mm, "end": v(-28.58, 244.48) * mm});
            skLineSegment(sketch, "E12.direction1", {"start": v(-142.87, 22.23) * mm, "end": v(-111.12, 22.23) * mm, "construction": true});
            skLineSegment(sketch, "E12.direction2", {"start": v(-142.87, 22.23) * mm, "end": v(-142.87, 53.98) * mm, "construction": true});
            skSolve(sketch);
        }
        {
            var Q0;
            Q0=makeQuery(id+"F6.imprint","IMPRINT",FACE,{"disambiguationData":[TD([[makeQuery(id+"F6.imprint","IMPRINT",EDGE,{"derivedFrom":sQuery(id+"F6.wireOp",EDGE,"E2.bottom")}),-1.0]])]});
            var Q1;
            Q1=makeQuery(id+"F6.imprint","IMPRINT",FACE,{"disambiguationData":[TD([[makeQuery(id+"F6.imprint","IMPRINT",EDGE,{"derivedFrom":sQuery(id+"F6.wireOp",EDGE,"E3.bottom")}),-1.0]])]});
            var Q2;
            Q2=makeQuery(id+"F6.imprint","IMPRINT",FACE,{"disambiguationData":[TD([[makeQuery(id+"F6.imprint","IMPRINT",EDGE,{"derivedFrom":sQuery(id+"F6.wireOp",EDGE,"E4.bottom")}),1.0]])]});
            var Q3;
            Q3=makeQuery(id+"F6.imprint","IMPRINT",FACE,{"disambiguationData":[TD([[makeQuery(id+"F6.imprint","IMPRINT",EDGE,{"derivedFrom":sQuery(id+"F6.wireOp",EDGE,"E5.bottom")}),-1.0]])]});
            var Q4;
            Q4=makeQuery(id+"F6.imprint","IMPRINT",FACE,{"disambiguationData":[TD([[makeQuery(id+"F6.imprint","IMPRINT",EDGE,{"derivedFrom":sQuery(id+"F6.wireOp",EDGE,"E12.0.7.0")}),1.0]])]});
            var Q5;
            Q5=makeQuery(id+"F6.imprint","IMPRINT",FACE,{"disambiguationData":[TD([[makeQuery(id+"F6.imprint","IMPRINT",EDGE,{"derivedFrom":sQuery(id+"F6.wireOp",EDGE,"E12.1.7.0")}),1.0]])]});
            var Q6;
            Q6=makeQuery(id+"F6.imprint","IMPRINT",FACE,{"disambiguationData":[TD([[makeQuery(id+"F6.imprint","IMPRINT",EDGE,{"derivedFrom":sQuery(id+"F6.wireOp",EDGE,"E12.2.7.0")}),1.0]])]});
            var Q7;
            Q7=makeQuery(id+"F6.imprint","IMPRINT",FACE,{"disambiguationData":[TD([[makeQuery(id+"F6.imprint","IMPRINT",EDGE,{"derivedFrom":sQuery(id+"F6.wireOp",EDGE,"E12.3.7.0")}),1.0]])]});
            var Q8;
            Q8=makeQuery(id+"F6.imprint","IMPRINT",FACE,{"disambiguationData":[TD([[makeQuery(id+"F6.imprint","IMPRINT",EDGE,{"derivedFrom":sQuery(id+"F6.wireOp",EDGE,"E12.3.6.0")}),1.0]])]});
            var Q9;
            Q9=makeQuery(id+"F6.imprint","IMPRINT",FACE,{"disambiguationData":[TD([[makeQuery(id+"F6.imprint","IMPRINT",EDGE,{"derivedFrom":sQuery(id+"F6.wireOp",EDGE,"E12.2.6.0")}),1.0]])]});
            var Q10;
            Q10=makeQuery(id+"F6.imprint","IMPRINT",FACE,{"disambiguationData":[TD([[makeQuery(id+"F6.imprint","IMPRINT",EDGE,{"derivedFrom":sQuery(id+"F6.wireOp",EDGE,"E12.1.6.0")}),1.0]])]});
            var Q11;
            Q11=makeQuery(id+"F6.imprint","IMPRINT",FACE,{"disambiguationData":[TD([[makeQuery(id+"F6.imprint","IMPRINT",EDGE,{"derivedFrom":sQuery(id+"F6.wireOp",EDGE,"E12.0.6.0")}),1.0]])]});
            var Q12;
            Q12=makeQuery(id+"F6.imprint","IMPRINT",FACE,{"disambiguationData":[TD([[makeQuery(id+"F6.imprint","IMPRINT",EDGE,{"derivedFrom":sQuery(id+"F6.wireOp",EDGE,"E12.0.5.0")}),1.0]])]});
            var Q13;
            Q13=makeQuery(id+"F6.imprint","IMPRINT",FACE,{"disambiguationData":[TD([[makeQuery(id+"F6.imprint","IMPRINT",EDGE,{"derivedFrom":sQuery(id+"F6.wireOp",EDGE,"E12.1.5.0")}),1.0]])]});
            var Q14;
            Q14=makeQuery(id+"F6.imprint","IMPRINT",FACE,{"disambiguationData":[TD([[makeQuery(id+"F6.imprint","IMPRINT",EDGE,{"derivedFrom":sQuery(id+"F6.wireOp",EDGE,"E12.2.5.0")}),1.0]])]});
            var Q15;
            Q15=makeQuery(id+"F6.imprint","IMPRINT",FACE,{"disambiguationData":[TD([[makeQuery(id+"F6.imprint","IMPRINT",EDGE,{"derivedFrom":sQuery(id+"F6.wireOp",EDGE,"E12.3.5.0")}),1.0]])]});
            var Q16;
            Q16=makeQuery(id+"F6.imprint","IMPRINT",FACE,{"disambiguationData":[TD([[makeQuery(id+"F6.imprint","IMPRINT",EDGE,{"derivedFrom":sQuery(id+"F6.wireOp",EDGE,"E12.0.4.0")}),1.0]])]});
            var Q17;
            Q17=makeQuery(id+"F6.imprint","IMPRINT",FACE,{"disambiguationData":[TD([[makeQuery(id+"F6.imprint","IMPRINT",EDGE,{"derivedFrom":sQuery(id+"F6.wireOp",EDGE,"E12.1.4.0")}),1.0]])]});
            var Q18;
            Q18=makeQuery(id+"F6.imprint","IMPRINT",FACE,{"disambiguationData":[TD([[makeQuery(id+"F6.imprint","IMPRINT",EDGE,{"derivedFrom":sQuery(id+"F6.wireOp",EDGE,"E12.2.4.0")}),1.0]])]});
            var Q19;
            Q19=makeQuery(id+"F6.imprint","IMPRINT",FACE,{"disambiguationData":[TD([[makeQuery(id+"F6.imprint","IMPRINT",EDGE,{"derivedFrom":sQuery(id+"F6.wireOp",EDGE,"E12.3.4.0")}),1.0]])]});
            var Q20;
            Q20=makeQuery(id+"F6.imprint","IMPRINT",FACE,{"disambiguationData":[TD([[makeQuery(id+"F6.imprint","IMPRINT",EDGE,{"derivedFrom":sQuery(id+"F6.wireOp",EDGE,"E12.3.3.0")}),1.0]])]});
            var Q21;
            Q21=makeQuery(id+"F6.imprint","IMPRINT",FACE,{"disambiguationData":[TD([[makeQuery(id+"F6.imprint","IMPRINT",EDGE,{"derivedFrom":sQuery(id+"F6.wireOp",EDGE,"E12.2.3.0")}),1.0]])]});
            var Q22;
            Q22=makeQuery(id+"F6.imprint","IMPRINT",FACE,{"disambiguationData":[TD([[makeQuery(id+"F6.imprint","IMPRINT",EDGE,{"derivedFrom":sQuery(id+"F6.wireOp",EDGE,"E12.1.3.0")}),1.0]])]});
            var Q23;
            Q23=makeQuery(id+"F6.imprint","IMPRINT",FACE,{"disambiguationData":[TD([[makeQuery(id+"F6.imprint","IMPRINT",EDGE,{"derivedFrom":sQuery(id+"F6.wireOp",EDGE,"E12.0.3.0")}),1.0]])]});
            var Q24;
            Q24=makeQuery(id+"F6.imprint","IMPRINT",FACE,{"disambiguationData":[TD([[makeQuery(id+"F6.imprint","IMPRINT",EDGE,{"derivedFrom":sQuery(id+"F6.wireOp",EDGE,"E12.0.2.0")}),1.0]])]});
            var Q25;
            Q25=makeQuery(id+"F6.imprint","IMPRINT",FACE,{"disambiguationData":[TD([[makeQuery(id+"F6.imprint","IMPRINT",EDGE,{"derivedFrom":sQuery(id+"F6.wireOp",EDGE,"E12.1.2.0")}),1.0]])]});
            var Q26;
            Q26=makeQuery(id+"F6.imprint","IMPRINT",FACE,{"disambiguationData":[TD([[makeQuery(id+"F6.imprint","IMPRINT",EDGE,{"derivedFrom":sQuery(id+"F6.wireOp",EDGE,"E12.2.2.0")}),1.0]])]});
            var Q27;
            Q27=makeQuery(id+"F6.imprint","IMPRINT",FACE,{"disambiguationData":[TD([[makeQuery(id+"F6.imprint","IMPRINT",EDGE,{"derivedFrom":sQuery(id+"F6.wireOp",EDGE,"E12.3.2.0")}),1.0]])]});
            var Q28;
            Q28=makeQuery(id+"F6.imprint","IMPRINT",FACE,{"disambiguationData":[TD([[makeQuery(id+"F6.imprint","IMPRINT",EDGE,{"derivedFrom":sQuery(id+"F6.wireOp",EDGE,"E12.3.1.0")}),1.0]])]});
            var Q29;
            Q29=makeQuery(id+"F6.imprint","IMPRINT",FACE,{"disambiguationData":[TD([[makeQuery(id+"F6.imprint","IMPRINT",EDGE,{"derivedFrom":sQuery(id+"F6.wireOp",EDGE,"E12.2.1.0")}),1.0]])]});
            var Q30;
            Q30=makeQuery(id+"F6.imprint","IMPRINT",FACE,{"disambiguationData":[TD([[makeQuery(id+"F6.imprint","IMPRINT",EDGE,{"derivedFrom":sQuery(id+"F6.wireOp",EDGE,"E12.1.1.0")}),1.0]])]});
            var Q31;
            Q31=makeQuery(id+"F6.imprint","IMPRINT",FACE,{"disambiguationData":[TD([[makeQuery(id+"F6.imprint","IMPRINT",EDGE,{"derivedFrom":sQuery(id+"F6.wireOp",EDGE,"E12.0.1.0")}),1.0]])]});
            var Q32;
            Q32=makeQuery(id+"F6.imprint","IMPRINT",FACE,{"disambiguationData":[TD([[makeQuery(id+"F6.imprint","IMPRINT",EDGE,{"derivedFrom":sQuery(id+"F6.wireOp",EDGE,"E6.bottom")}),-1.0]])]});
            var Q33;
            Q33=makeQuery(id+"F6.imprint","IMPRINT",FACE,{"disambiguationData":[TD([[makeQuery(id+"F6.imprint","IMPRINT",EDGE,{"derivedFrom":sQuery(id+"F6.wireOp",EDGE,"E12.1.0.0")}),1.0]])]});
            var Q34;
            Q34=makeQuery(id+"F6.imprint","IMPRINT",FACE,{"disambiguationData":[TD([[makeQuery(id+"F6.imprint","IMPRINT",EDGE,{"derivedFrom":sQuery(id+"F6.wireOp",EDGE,"E12.2.0.0")}),1.0]])]});
            var Q35;
            Q35=makeQuery(id+"F6.imprint","IMPRINT",FACE,{"disambiguationData":[TD([[makeQuery(id+"F6.imprint","IMPRINT",EDGE,{"derivedFrom":sQuery(id+"F6.wireOp",EDGE,"E12.3.0.0")}),1.0]])]});
            extrude(context, id + "F7", {"entities" : qUnion([Q0, Q1, Q2, Q3, Q4, Q5, Q6, Q7, Q8, Q9, Q10, Q11, Q12, Q13, Q14, Q15, Q16, Q17, Q18, Q19, Q20, Q21, Q22, Q23, Q24, Q25, Q26, Q27, Q28, Q29, Q30, Q31, Q32, Q33, Q34, Q35]), "operationType" : NewBodyOperationType.REMOVE, "oppositeDirection" : true, "depth" : 3.17 * mm});
        }
    });
